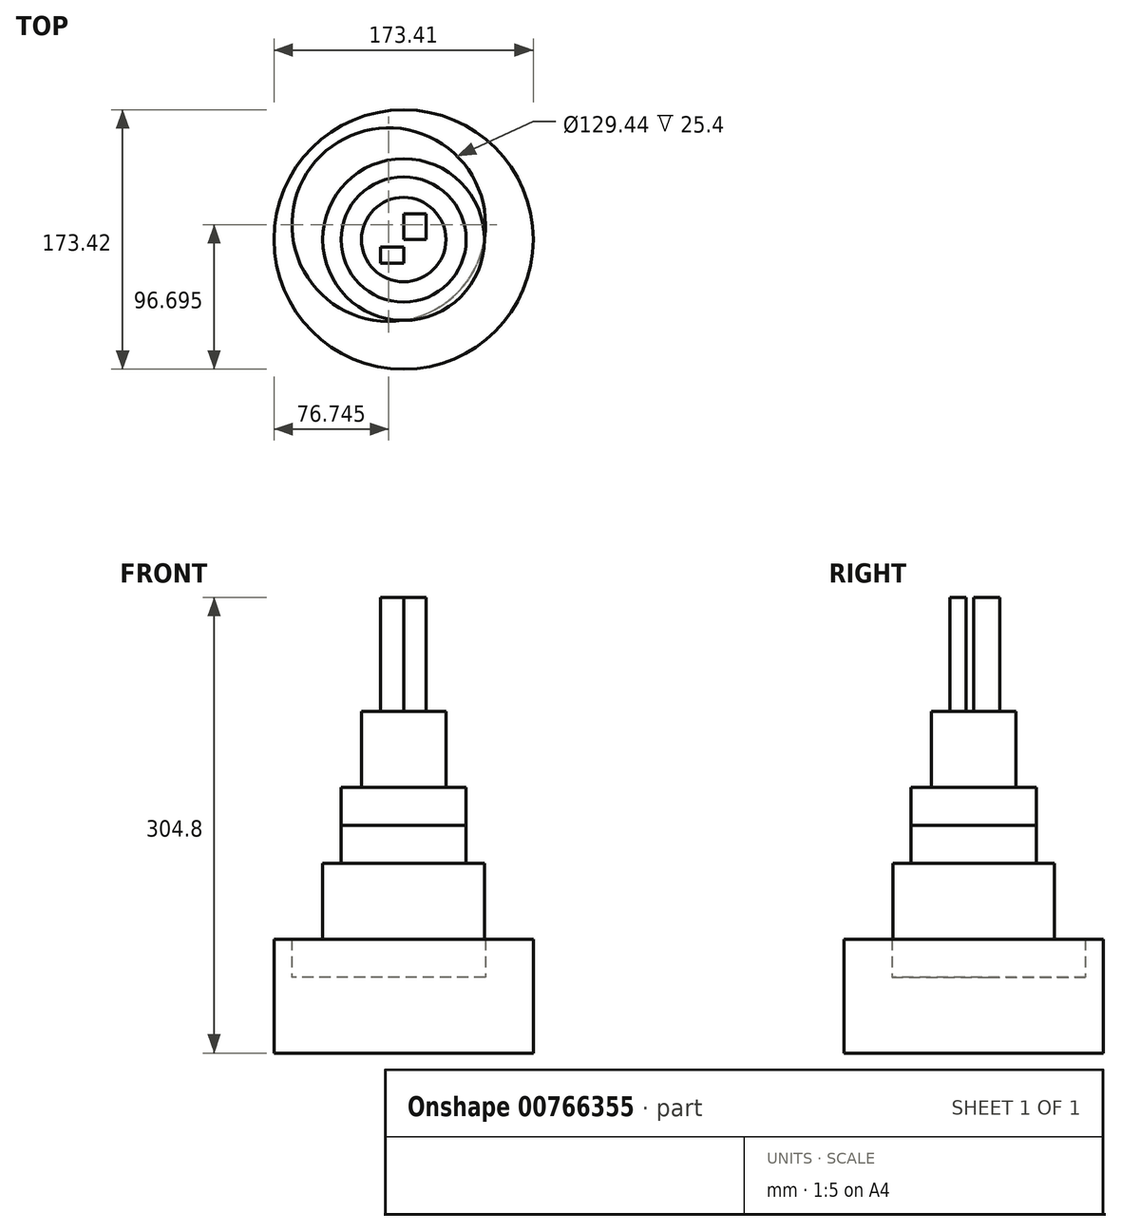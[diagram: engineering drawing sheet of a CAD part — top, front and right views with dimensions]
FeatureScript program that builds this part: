
annotation { "Feature Type Name" : "Feature", "Feature Type Description" : "" }
export const myFeature = defineFeature(function(context is Context, id is Id, definition is map)
    precondition{}
    {
        {
            var Q0;
            Q0=qCreatedBy(makeId("Top.planeOp"),FACE);
            var sketch = newSketch(context, id + "F0", { "sketchPlane" : qUnion([Q0])});
            skCircle(sketch, "E0", {"center": v(-14.92, 15.85) * mm, "radius": 86.7 * mm});
            skSolve(sketch);
        }
        {
            var Q0;
            Q0 = qSketchRegion(id + "F0", true);
            extrude(context, id + "F1", {"entities" : qUnion([Q0]), "depth" : 50.8 * mm, "offsetDistance" : 25.4 * mm});
        }
        {
            var Q0;
            Q0=makeQuery(id+"F1.opExtrude","CAP_FACE",FACE,{"disambiguationData":[OSD([sQuery(id+"F0.wireOp",EDGE,"E0")])],"isStart":false});
            var sketch = newSketch(context, id + "F2", { "sketchPlane" : qUnion([Q0])});
            skCircle(sketch, "E1", {"center": v(-24.88, 25.84) * mm, "radius": 64.72 * mm});
            skSolve(sketch);
        }
        {
            var Q0;
            Q0 = qSketchRegion(id + "F0", true);
            extrude(context, id + "F3", {"entities" : qUnion([Q0]), "operationType" : NewBodyOperationType.ADD, "depth" : 25.4 * mm, "offsetDistance" : 25.4 * mm});
        }
        {
            var Q0;
            Q0=makeQuery(id+"F2.imprint","IMPRINT",FACE,{"disambiguationData":[TD([[makeQuery(id+"F2.imprint","IMPRINT",EDGE,{"derivedFrom":makeQuery(id+"F1.opExtrude","CAP_EDGE",EDGE,{"disambiguationData":[OSD([sQuery(id+"F0.wireOp",EDGE,"E0")])],"isStart":false})}),1.0]])]});
            extrude(context, id + "F4", {"entities" : qUnion([Q0]), "operationType" : NewBodyOperationType.ADD, "depth" : 25.4 * mm, "offsetDistance" : 25.4 * mm});
        }
        {
            var Q0;
            Q0=makeQuery(id+"F4.opExtrude","CAP_FACE",FACE,{"disambiguationData":[OSD([sQuery(id+"F0.wireOp",EDGE,"E0"),sQuery(id+"F2.wireOp",EDGE,"E1")])],"isStart":false});
            var sketch = newSketch(context, id + "F5", { "sketchPlane" : qUnion([Q0])});
            skCircle(sketch, "E2", {"center": v(-14.92, 15.85) * mm, "radius": 54.06 * mm});
            skSolve(sketch);
        }
        {
            var Q0;
            Q0 = qSketchRegion(id + "F5", true);
            extrude(context, id + "F6", {"entities" : qUnion([Q0]), "depth" : 50.8 * mm, "offsetDistance" : 25.4 * mm});
        }
        {
            var Q0;
            Q0=makeQuery(id+"F6.opExtrude","CAP_FACE",FACE,{"disambiguationData":[OSD([sQuery(id+"F5.wireOp",EDGE,"E2")])],"isStart":false});
            var sketch = newSketch(context, id + "F7", { "sketchPlane" : qUnion([Q0])});
            skCircle(sketch, "E3", {"center": v(-14.92, 15.85) * mm, "radius": 41.84 * mm});
            skSolve(sketch);
        }
        {
            var Q0;
            Q0 = qSketchRegion(id + "F7", true);
            extrude(context, id + "F8", {"entities" : qUnion([Q0]), "depth" : 50.8 * mm, "offsetDistance" : 25.4 * mm});
        }
        {
            var Q0;
            Q0 = qSketchRegion(id + "F7", true);
            extrude(context, id + "F9", {"entities" : qUnion([Q0]), "depth" : 25.4 * mm, "offsetDistance" : 25.4 * mm});
        }
        {
            var Q0;
            Q0=makeQuery(id+"F8.opExtrude","CAP_FACE",FACE,{"disambiguationData":[OSD([sQuery(id+"F7.wireOp",EDGE,"E3")])],"isStart":false});
            var sketch = newSketch(context, id + "F10", { "sketchPlane" : qUnion([Q0])});
            skCircle(sketch, "E4", {"center": v(-14.92, 15.85) * mm, "radius": 28.2 * mm});
            skSolve(sketch);
        }
        {
            var Q0;
            Q0 = qSketchRegion(id + "F10", true);
            extrude(context, id + "F11", {"entities" : qUnion([Q0]), "operationType" : NewBodyOperationType.ADD, "depth" : 50.8 * mm, "offsetDistance" : 25.4 * mm});
        }
        {
            var Q0;
            Q0=makeQuery(id+"F11.opExtrude","CAP_FACE",FACE,{"disambiguationData":[OSD([sQuery(id+"F10.wireOp",EDGE,"E4")])],"isStart":false});
            var sketch = newSketch(context, id + "F12", { "sketchPlane" : qUnion([Q0])});
            skLineSegment(sketch, "E5.bottom", {"start": v(-14.92, 15.85) * mm, "end": v(0, 15.85) * mm});
            skLineSegment(sketch, "E5.top", {"start": v(-14.92, 33.21) * mm, "end": v(0, 33.21) * mm});
            skLineSegment(sketch, "E5.left", {"start": v(-14.92, 15.85) * mm, "end": v(-14.92, 33.21) * mm});
            skLineSegment(sketch, "E5.right", {"start": v(0, 15.85) * mm, "end": v(0, 33.21) * mm});
            skSolve(sketch);
        }
        {
            var Q0;
            Q0 = qSketchRegion(id + "F12", true);
            extrude(context, id + "F13", {"entities" : qUnion([Q0]), "operationType" : NewBodyOperationType.ADD, "depth" : 76.2 * mm, "offsetDistance" : 25.4 * mm});
        }
        {
            var Q0;
            Q0=makeQuery(id+"F11.opExtrude","CAP_FACE",FACE,{"disambiguationData":[OSD([sQuery(id+"F10.wireOp",EDGE,"E4")])],"isStart":false});
            var sketch = newSketch(context, id + "F14", { "sketchPlane" : qUnion([Q0])});
            skLineSegment(sketch, "E6.bottom", {"start": v(-30.5, 10.9) * mm, "end": v(-14.92, 10.9) * mm});
            skLineSegment(sketch, "E6.top", {"start": v(-30.5, 0) * mm, "end": v(-14.92, 0) * mm});
            skLineSegment(sketch, "E6.left", {"start": v(-30.5, 10.9) * mm, "end": v(-30.5, 0) * mm});
            skLineSegment(sketch, "E6.right", {"start": v(-14.92, 10.9) * mm, "end": v(-14.92, 0) * mm});
            skSolve(sketch);
        }
        {
            var Q0;
            Q0 = qSketchRegion(id + "F14", true);
            extrude(context, id + "F15", {"entities" : qUnion([Q0]), "operationType" : NewBodyOperationType.ADD, "depth" : 76.2 * mm, "offsetDistance" : 25.4 * mm});
        }
    });
